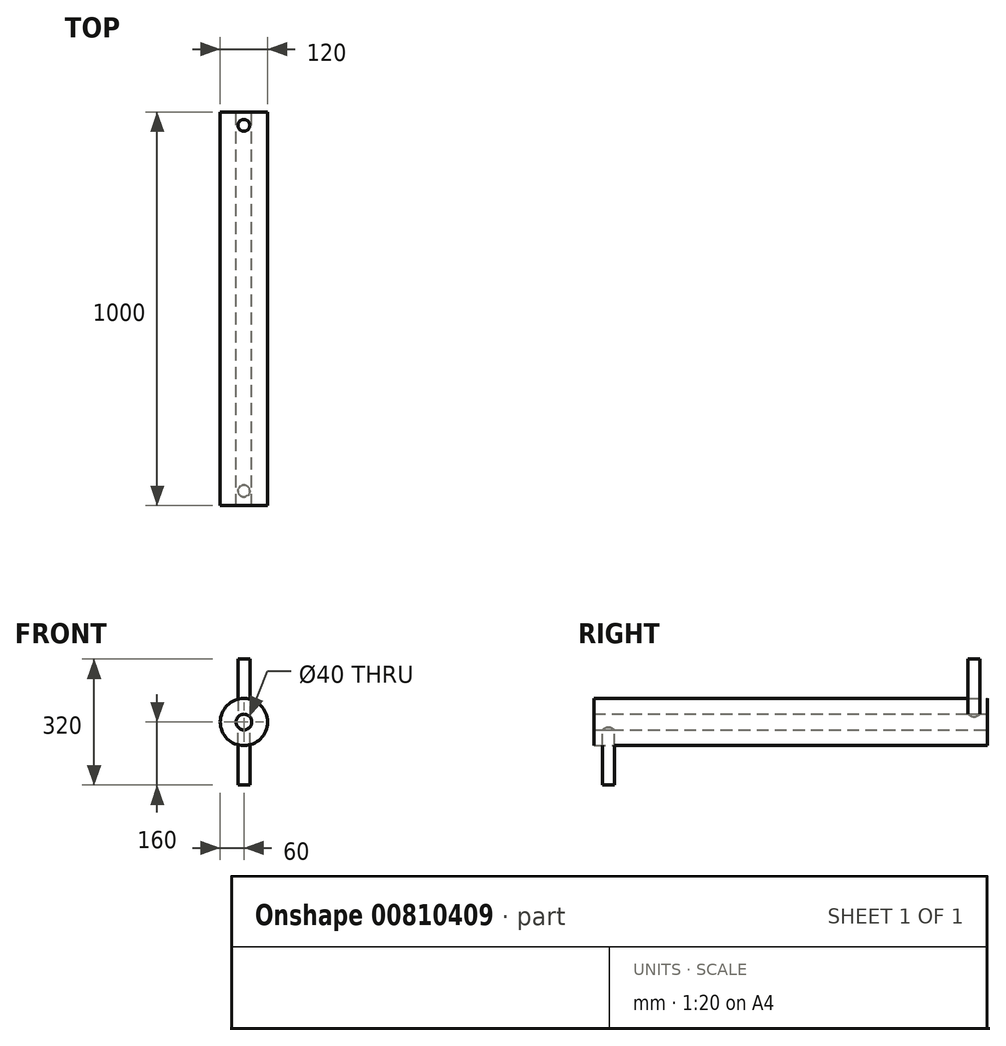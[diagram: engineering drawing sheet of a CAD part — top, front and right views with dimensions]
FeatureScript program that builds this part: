
annotation { "Feature Type Name" : "Feature", "Feature Type Description" : "" }
export const myFeature = defineFeature(function(context is Context, id is Id, definition is map)
    precondition{}
    {
        {
            var Q0;
            Q0=qCreatedBy(makeId("Front.planeOp"),FACE);
            var sketch = newSketch(context, id + "F0", { "sketchPlane" : qUnion([Q0])});
            skCircle(sketch, "E0", {"center": v(0, 0) * mm, "radius": 60 * mm});
            skSolve(sketch);
        }
        {
            var Q0;
            Q0=qCreatedBy(makeId("Front.planeOp"),FACE);
            var sketch = newSketch(context, id + "F1", { "sketchPlane" : qUnion([Q0])});
            skCircle(sketch, "E1", {"center": v(0, 0) * mm, "radius": 20 * mm});
            skSolve(sketch);
        }
        {
            var Q0;
            Q0=makeQuery(id+"F0.imprint","IMPRINT",FACE,{"disambiguationData":[TD([[makeQuery(id+"F0.imprint","IMPRINT",EDGE,{"derivedFrom":sQuery(id+"F0.wireOp",EDGE,"E0")}),1.0]])]});
            extrude(context, id + "F2", {"entities" : qUnion([Q0]), "depth" : 1000 * mm, "offsetDistance" : 25 * mm});
        }
        {
            var Q0;
            Q0=qCreatedBy(makeId("Top.planeOp"),FACE);
            var sketch = newSketch(context, id + "F3", { "sketchPlane" : qUnion([Q0])});
            skCircle(sketch, "E2", {"center": v(0, -33.89) * mm, "radius": 15 * mm});
            skSolve(sketch);
        }
        {
            var Q0;
            Q0=qSketchRegion(id+"F3",true);
            extrude(context, id + "F4", {"entities" : qUnion([Q0]), "depth" : 160 * mm, "offsetDistance" : 25 * mm});
        }
        {
            var Q0;
            Q0=qCreatedBy(makeId("Top.planeOp"),FACE);
            var sketch = newSketch(context, id + "F5", { "sketchPlane" : qUnion([Q0])});
            skCircle(sketch, "E3", {"center": v(0, -962.96) * mm, "radius": 15 * mm});
            skSolve(sketch);
        }
        {
            var Q0;
            Q0=qSketchRegion(id+"F5",true);
            extrude(context, id + "F6", {"entities" : qUnion([Q0]), "oppositeDirection" : true, "depth" : 160 * mm, "offsetDistance" : 25 * mm});
        }
        {
            var Q0;
            Q0 = qSketchRegion(id + "F1", true);
            var Q1;
            Q1=sQuery(id+"F1.wireOp",EDGE,"E1");
            extrude(context, id + "F7", {"entities" : qUnion([Q0]), "operationType" : NewBodyOperationType.REMOVE, "surfaceEntities" : qUnion([Q1]), "depth" : 1000 * mm, "offsetDistance" : 25 * mm});
        }
    });
